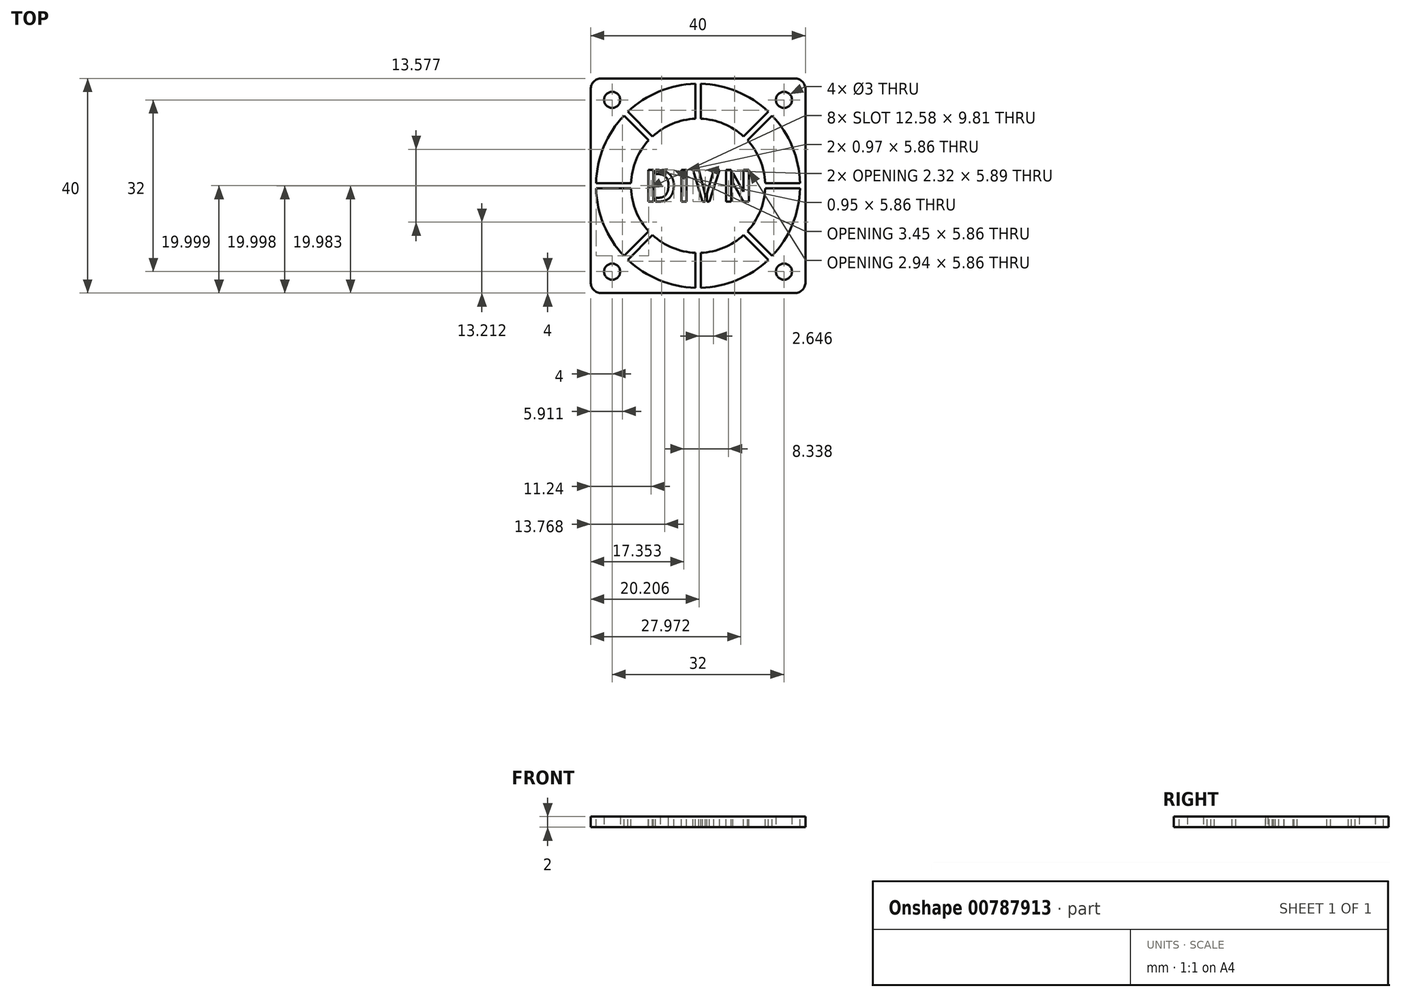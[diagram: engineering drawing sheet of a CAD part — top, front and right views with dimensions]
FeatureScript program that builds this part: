
annotation { "Feature Type Name" : "Feature", "Feature Type Description" : "" }
export const myFeature = defineFeature(function(context is Context, id is Id, definition is map)
    precondition{}
    {
        {
            var Q0;
            Q0=qCreatedBy(makeId("Top.planeOp"),FACE);
            var sketch = newSketch(context, id + "F0", { "sketchPlane" : qUnion([Q0])});
            skLineSegment(sketch, "E0.bottom", {"start": v(18, 20) * mm, "end": v(-18, 20) * mm});
            skLineSegment(sketch, "E0.top", {"start": v(18, -20) * mm, "end": v(-18, -20) * mm});
            skLineSegment(sketch, "E0.left", {"start": v(20, 18) * mm, "end": v(20, -18) * mm});
            skLineSegment(sketch, "E0.right", {"start": v(-20, 18) * mm, "end": v(-20, -18) * mm});
            skPoint(sketch, "E0.middle", {"position": v(0, 0) * mm});
            skPoint(sketch, "E1.visualSharp", {"position": v(-20, 20) * mm});
            skArc(sketch, "E1.filletArc", {"start": v(-18, 20) * mm, "mid": v(-19.41, 19.41) * mm, "end": v(-20, 18) * mm});
            skPoint(sketch, "E2.visualSharp", {"position": v(20, 20) * mm});
            skArc(sketch, "E2.filletArc", {"start": v(20, 18) * mm, "mid": v(19.41, 19.41) * mm, "end": v(18, 20) * mm});
            skPoint(sketch, "E3.visualSharp", {"position": v(20, -20) * mm});
            skArc(sketch, "E3.filletArc", {"start": v(18, -20) * mm, "mid": v(19.41, -19.41) * mm, "end": v(20, -18) * mm});
            skPoint(sketch, "E4.visualSharp", {"position": v(-20, -20) * mm});
            skArc(sketch, "E4.filletArc", {"start": v(-20, -18) * mm, "mid": v(-19.41, -19.41) * mm, "end": v(-18, -20) * mm});
            skCircle(sketch, "E5", {"center": v(-16, 16) * mm, "radius": 1.5 * mm});
            skCircle(sketch, "E6", {"center": v(16, 16) * mm, "radius": 1.5 * mm});
            skCircle(sketch, "E7", {"center": v(16, -16) * mm, "radius": 1.5 * mm});
            skCircle(sketch, "E8", {"center": v(-16, -16) * mm, "radius": 1.5 * mm});
            skSolve(sketch);
        }
        {
            var Q0;
            Q0=makeQuery(id+"F0.imprint","IMPRINT",FACE,{"disambiguationData":[TD([[makeQuery(id+"F0.imprint","IMPRINT",EDGE,{"derivedFrom":sQuery(id+"F0.wireOp",EDGE,"E0.bottom")}),1.0]])]});
            extrude(context, id + "F1", {"entities" : qUnion([Q0]), "depth" : 2 * mm, "offsetDistance" : 25 * mm});
        }
        {
            var Q0;
            Q0=makeQuery(id+"F1.opExtrude","CAP_FACE",FACE,{"disambiguationData":[OSD([sQuery(id+"F0.wireOp",EDGE,"E0.bottom"),sQuery(id+"F0.wireOp",EDGE,"E0.top"),sQuery(id+"F0.wireOp",EDGE,"E0.left"),sQuery(id+"F0.wireOp",EDGE,"E0.right"),sQuery(id+"F0.wireOp",EDGE,"E1.filletArc"),sQuery(id+"F0.wireOp",EDGE,"E2.filletArc"),sQuery(id+"F0.wireOp",EDGE,"E3.filletArc"),sQuery(id+"F0.wireOp",EDGE,"E4.filletArc"),sQuery(id+"F0.wireOp",EDGE,"E5"),sQuery(id+"F0.wireOp",EDGE,"E6"),sQuery(id+"F0.wireOp",EDGE,"E7"),sQuery(id+"F0.wireOp",EDGE,"E8")])],"isStart":false});
            var sketch = newSketch(context, id + "F2", { "sketchPlane" : qUnion([Q0])});
            skCircle(sketch, "E9", {"center": v(0, 0) * mm, "radius": 12.5 * mm});
            skCircle(sketch, "E10", {"center": v(0, 0) * mm, "radius": 19 * mm});
            skText(sketch, "E11", { "text": "DIVN", "fontName": "AllertaStencil-Regular.ttf"});
            const initialGuessF2  = {"E11": [-0.01, -0.00293, 1, 0, 0.00586]};
            skSetInitialGuess(sketch, initialGuessF2);
            skSolve(sketch);
        }
        {
            var Q0;
            Q0=makeQuery(id+"F2.imprint","IMPRINT",FACE,{"disambiguationData":[TD([[makeQuery(id+"F2.imprint","IMPRINT",EDGE,{"derivedFrom":sQuery(id+"F2.wireOp",EDGE,"E9")}),-1.0]])]});
            var Q1;
            Q1=makeQuery(id+"F2.imprint","IMPRINT",FACE,{"disambiguationData":[TD([[makeQuery(id+"F2.imprint","IMPRINT",EDGE,{"derivedFrom":sQuery(id+"F2.wireOp",EDGE,"E11.sketch_text.stroke-0")}),-1.0]])]});
            var Q2;
            Q2=makeQuery(id+"F2.imprint","IMPRINT",FACE,{"disambiguationData":[TD([[makeQuery(id+"F2.imprint","IMPRINT",EDGE,{"derivedFrom":sQuery(id+"F2.wireOp",EDGE,"E11.sketch_text.stroke-4")}),-1.0]])]});
            var Q3;
            Q3=makeQuery(id+"F2.imprint","IMPRINT",FACE,{"disambiguationData":[TD([[makeQuery(id+"F2.imprint","IMPRINT",EDGE,{"derivedFrom":sQuery(id+"F2.wireOp",EDGE,"E11.sketch_text.stroke-26")}),-1.0]])]});
            var Q4;
            Q4=makeQuery(id+"F2.imprint","IMPRINT",FACE,{"disambiguationData":[TD([[makeQuery(id+"F2.imprint","IMPRINT",EDGE,{"derivedFrom":sQuery(id+"F2.wireOp",EDGE,"E11.sketch_text.stroke-30")}),-1.0]])]});
            var Q5;
            Q5=makeQuery(id+"F2.imprint","IMPRINT",FACE,{"disambiguationData":[TD([[makeQuery(id+"F2.imprint","IMPRINT",EDGE,{"derivedFrom":sQuery(id+"F2.wireOp",EDGE,"E11.sketch_text.stroke-35")}),-1.0]])]});
            var Q6;
            Q6=makeQuery(id+"F2.imprint","IMPRINT",FACE,{"disambiguationData":[TD([[makeQuery(id+"F2.imprint","IMPRINT",EDGE,{"derivedFrom":sQuery(id+"F2.wireOp",EDGE,"E11.sketch_text.stroke-47")}),-1.0]])]});
            var Q7;
            Q7=makeQuery(id+"F2.imprint","IMPRINT",FACE,{"disambiguationData":[TD([[makeQuery(id+"F2.imprint","IMPRINT",EDGE,{"derivedFrom":sQuery(id+"F2.wireOp",EDGE,"E11.sketch_text.stroke-40")}),-1.0]])]});
            extrude(context, id + "F3", {"entities" : qUnion([Q0, Q1, Q2, Q3, Q4, Q5, Q6, Q7]), "operationType" : NewBodyOperationType.REMOVE, "oppositeDirection" : true, "depth" : 2 * mm, "offsetDistance" : 25 * mm});
        }
        {
            var Q0;
            Q0=makeQuery(id+"F3.boolean.opBoolean","SPLIT",FACE,{"disambiguationData":[TD([makeQuery(id+"F3.opExtrude","SWEPT_FACE",FACE,{"disambiguationData":[OSD([sQuery(id+"F2.wireOp",EDGE,"E9")])]})])],"derivedFrom":makeQuery(id+"F1.opExtrude","CAP_FACE",FACE,{"disambiguationData":[OSD([sQuery(id+"F0.wireOp",EDGE,"E0.bottom"),sQuery(id+"F0.wireOp",EDGE,"E0.top"),sQuery(id+"F0.wireOp",EDGE,"E0.left"),sQuery(id+"F0.wireOp",EDGE,"E0.right"),sQuery(id+"F0.wireOp",EDGE,"E1.filletArc"),sQuery(id+"F0.wireOp",EDGE,"E2.filletArc"),sQuery(id+"F0.wireOp",EDGE,"E3.filletArc"),sQuery(id+"F0.wireOp",EDGE,"E4.filletArc"),sQuery(id+"F0.wireOp",EDGE,"E5"),sQuery(id+"F0.wireOp",EDGE,"E6"),sQuery(id+"F0.wireOp",EDGE,"E7"),sQuery(id+"F0.wireOp",EDGE,"E8")])],"isStart":false})});
            var sketch = newSketch(context, id + "F4", { "sketchPlane" : qUnion([Q0])});
            skLineSegment(sketch, "E12", {"start": v(0, -25.11) * mm, "end": v(0, 26.68) * mm, "construction": true});
            skLineSegment(sketch, "E13", {"start": v(29.7, 0) * mm, "end": v(-31.45, 0) * mm, "construction": true});
            skLineSegment(sketch, "E14.bottom", {"start": v(-0.5, 19.1) * mm, "end": v(0.5, 19.1) * mm});
            skLineSegment(sketch, "E14.top", {"start": v(-0.5, 12.1) * mm, "end": v(0.5, 12.1) * mm});
            skLineSegment(sketch, "E14.left", {"start": v(-0.5, 19.1) * mm, "end": v(-0.5, 12.1) * mm});
            skLineSegment(sketch, "E14.right", {"start": v(0.5, 19.1) * mm, "end": v(0.5, 12.1) * mm});
            skLineSegment(sketch, "E15.1.0", {"start": v(-13.15, 13.86) * mm, "end": v(-8.2, 8.9) * mm});
            skLineSegment(sketch, "E15.1.1", {"start": v(-13.86, 13.15) * mm, "end": v(-8.9, 8.2) * mm});
            skLineSegment(sketch, "E15.1.2", {"start": v(-13.86, 13.15) * mm, "end": v(-13.15, 13.86) * mm});
            skLineSegment(sketch, "E15.1.3", {"start": v(-8.9, 8.2) * mm, "end": v(-8.2, 8.9) * mm});
            skLineSegment(sketch, "E15.2.0", {"start": v(-19.1, 0.5) * mm, "end": v(-12.1, 0.5) * mm});
            skLineSegment(sketch, "E15.2.1", {"start": v(-19.1, -0.5) * mm, "end": v(-12.1, -0.5) * mm});
            skLineSegment(sketch, "E15.2.2", {"start": v(-19.1, -0.5) * mm, "end": v(-19.1, 0.5) * mm});
            skLineSegment(sketch, "E15.2.3", {"start": v(-12.1, -0.5) * mm, "end": v(-12.1, 0.5) * mm});
            skLineSegment(sketch, "E15.3.0", {"start": v(-13.86, -13.15) * mm, "end": v(-8.9, -8.2) * mm});
            skLineSegment(sketch, "E15.3.1", {"start": v(-13.15, -13.86) * mm, "end": v(-8.2, -8.9) * mm});
            skLineSegment(sketch, "E15.3.2", {"start": v(-13.15, -13.86) * mm, "end": v(-13.86, -13.15) * mm});
            skLineSegment(sketch, "E15.3.3", {"start": v(-8.2, -8.9) * mm, "end": v(-8.9, -8.2) * mm});
            skLineSegment(sketch, "E15.4.0", {"start": v(-0.5, -19.1) * mm, "end": v(-0.5, -12.1) * mm});
            skLineSegment(sketch, "E15.4.1", {"start": v(0.5, -19.1) * mm, "end": v(0.5, -12.1) * mm});
            skLineSegment(sketch, "E15.4.2", {"start": v(0.5, -19.1) * mm, "end": v(-0.5, -19.1) * mm});
            skLineSegment(sketch, "E15.4.3", {"start": v(0.5, -12.1) * mm, "end": v(-0.5, -12.1) * mm});
            skLineSegment(sketch, "E15.5.0", {"start": v(13.15, -13.86) * mm, "end": v(8.2, -8.9) * mm});
            skLineSegment(sketch, "E15.5.1", {"start": v(13.86, -13.15) * mm, "end": v(8.9, -8.2) * mm});
            skLineSegment(sketch, "E15.5.2", {"start": v(13.86, -13.15) * mm, "end": v(13.15, -13.86) * mm});
            skLineSegment(sketch, "E15.5.3", {"start": v(8.9, -8.2) * mm, "end": v(8.2, -8.9) * mm});
            skLineSegment(sketch, "E15.6.0", {"start": v(19.1, -0.5) * mm, "end": v(12.1, -0.5) * mm});
            skLineSegment(sketch, "E15.6.1", {"start": v(19.1, 0.5) * mm, "end": v(12.1, 0.5) * mm});
            skLineSegment(sketch, "E15.6.2", {"start": v(19.1, 0.5) * mm, "end": v(19.1, -0.5) * mm});
            skLineSegment(sketch, "E15.6.3", {"start": v(12.1, 0.5) * mm, "end": v(12.1, -0.5) * mm});
            skLineSegment(sketch, "E15.7.0", {"start": v(13.86, 13.15) * mm, "end": v(8.9, 8.2) * mm});
            skLineSegment(sketch, "E15.7.1", {"start": v(13.15, 13.86) * mm, "end": v(8.2, 8.9) * mm});
            skLineSegment(sketch, "E15.7.2", {"start": v(13.15, 13.86) * mm, "end": v(13.86, 13.15) * mm});
            skLineSegment(sketch, "E15.7.3", {"start": v(8.2, 8.9) * mm, "end": v(8.9, 8.2) * mm});
            skPoint(sketch, "E15.center", {"position": v(0, 0) * mm});
            skSolve(sketch);
        }
        {
            var Q0;
            {var subQ0=sQuery(id+"F4.wireOp",EDGE,"E14.bottom");Q0=makeQuery(id+"F4.imprint","IMPRINT",FACE,{"disambiguationData":[TD([[makeQuery(id+"F4.imprint","IMPRINT",EDGE,{"derivedFrom":subQ0}),-1.0]])]});}
            var Q1;
            {var subQ0=sQuery(id+"F4.wireOp",EDGE,"E15.7.2");Q1=makeQuery(id+"F4.imprint","IMPRINT",FACE,{"disambiguationData":[TD([[makeQuery(id+"F4.imprint","IMPRINT",EDGE,{"derivedFrom":subQ0}),-1.0]])]});}
            var Q2;
            {var subQ0=sQuery(id+"F4.wireOp",EDGE,"E15.6.2");Q2=makeQuery(id+"F4.imprint","IMPRINT",FACE,{"disambiguationData":[TD([[makeQuery(id+"F4.imprint","IMPRINT",EDGE,{"derivedFrom":subQ0}),-1.0]])]});}
            var Q3;
            {var subQ0=sQuery(id+"F4.wireOp",EDGE,"E15.5.2");Q3=makeQuery(id+"F4.imprint","IMPRINT",FACE,{"disambiguationData":[TD([[makeQuery(id+"F4.imprint","IMPRINT",EDGE,{"derivedFrom":subQ0}),-1.0]])]});}
            var Q4;
            {var subQ0=sQuery(id+"F4.wireOp",EDGE,"E15.4.2");Q4=makeQuery(id+"F4.imprint","IMPRINT",FACE,{"disambiguationData":[TD([[makeQuery(id+"F4.imprint","IMPRINT",EDGE,{"derivedFrom":subQ0}),-1.0]])]});}
            var Q5;
            {var subQ0=sQuery(id+"F4.wireOp",EDGE,"E15.3.2");Q5=makeQuery(id+"F4.imprint","IMPRINT",FACE,{"disambiguationData":[TD([[makeQuery(id+"F4.imprint","IMPRINT",EDGE,{"derivedFrom":subQ0}),-1.0]])]});}
            var Q6;
            {var subQ0=sQuery(id+"F4.wireOp",EDGE,"E15.2.2");Q6=makeQuery(id+"F4.imprint","IMPRINT",FACE,{"disambiguationData":[TD([[makeQuery(id+"F4.imprint","IMPRINT",EDGE,{"derivedFrom":subQ0}),-1.0]])]});}
            var Q7;
            {var subQ0=sQuery(id+"F4.wireOp",EDGE,"E15.1.2");Q7=makeQuery(id+"F4.imprint","IMPRINT",FACE,{"disambiguationData":[TD([[makeQuery(id+"F4.imprint","IMPRINT",EDGE,{"derivedFrom":subQ0}),-1.0]])]});}
            extrude(context, id + "F5", {"entities" : qUnion([Q0, Q1, Q2, Q3, Q4, Q5, Q6, Q7]), "operationType" : NewBodyOperationType.ADD, "oppositeDirection" : true, "depth" : 2 * mm, "offsetDistance" : 25 * mm});
        }
    });
